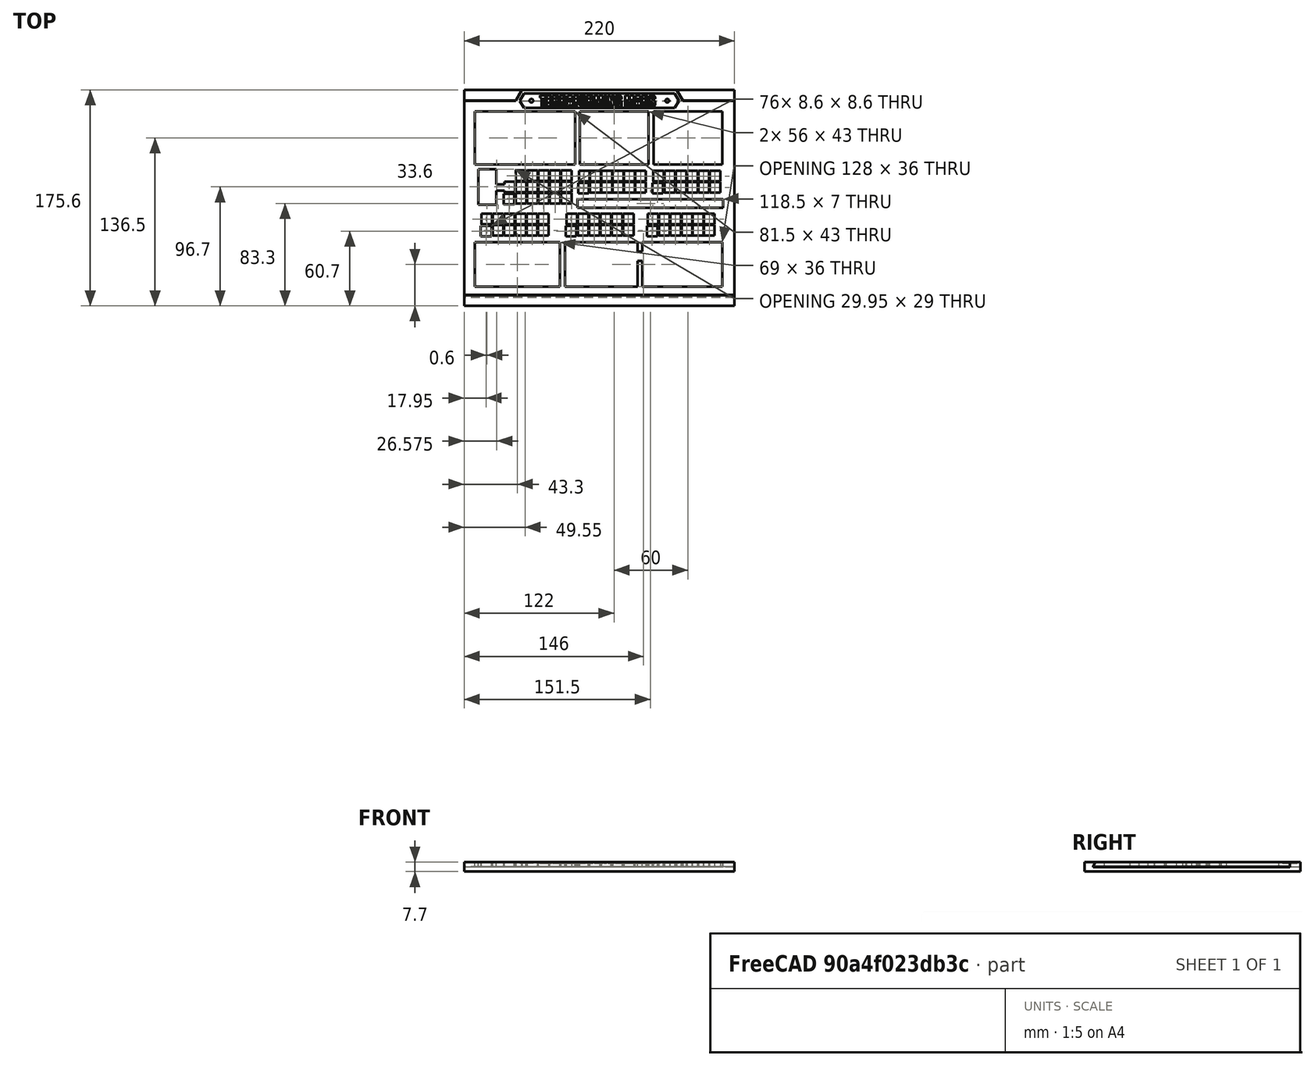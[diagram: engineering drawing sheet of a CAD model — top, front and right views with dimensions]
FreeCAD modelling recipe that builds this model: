
FCSTD DOCUMENT  (FreeCAD 0.21R33668 +26 (Git))
Label: overlay-full-v4
License: All rights reserved
LicenseURL: https://en.wikipedia.org/wiki/All_rights_reserved
objects: Sketcher::SketchObject×9, PartDesign::Pad×9, PartDesign::Pocket×4, Part::Feature×2, PartDesign::Body×2, Mesh::Feature×1, Part::Refine×1, PartDesign::FeatureBase×1, Part::Part2DObjectPython×1, Part::Extrusion×1
note: 43 computed .brp shape members not serialized (recipe doc carries the construction recipe); baked Part::Feature solids carry a one-line shape summary decoded from their .brp

FEATURE [Mesh::Feature] Terraforming_Mars_overlay
FEATURE [Part::Feature] Terraforming_Mars_overlay001
  shape: bbox 208 x 148 x 3.7 mm, 1736 faces, 0 solids (baked)
FEATURE [Part::Feature] Terraforming_Mars_overlay001_solid  label="Terraforming_Mars_overlay001 (Solid)"
  shape: bbox 208 x 148 x 3.7 mm, 1736 faces (baked)
FEATURE [Part::Refine] Terraforming_Mars_overlay001_solid001  label="Terraforming_Mars_overlay001 (Solid)001"
  Source = -> Terraforming_Mars_overlay001_solid
FEATURE [PartDesign::FeatureBase] BaseFeature
  BaseFeature = -> Terraforming_Mars_overlay001_solid001
FEATURE [Sketcher::SketchObject] Sketch
  ExternalGeometry = -> [BaseFeature]
  FullyConstrained = true
  MapMode = 5
  Placement = pos=(0,0,3.7) rot=(0,0,1;0rad)
  Support = -> [BaseFeature]
  sketch-geometry (8):
    g0: LineSegment StartX=6 StartY=154 StartZ=0 EndX=214 EndY=154 EndZ=0
    g1: LineSegment StartX=214 StartY=154 StartZ=0 EndX=214 EndY=6 EndZ=0
    g2: LineSegment StartX=214 StartY=6 StartZ=0 EndX=6 EndY=6 EndZ=0
    g3: LineSegment StartX=6 StartY=6 StartZ=0 EndX=6 EndY=154 EndZ=0
    g4: LineSegment StartX=0 StartY=160 StartZ=0 EndX=220 EndY=160 EndZ=0
    g5: LineSegment StartX=220 StartY=160 StartZ=0 EndX=220 EndY=0 EndZ=0
    g6: LineSegment StartX=220 StartY=0 StartZ=0 EndX=0 EndY=0 EndZ=0
    g7: LineSegment StartX=0 StartY=0 StartZ=0 EndX=0 EndY=160 EndZ=0
  constraints (22):
    c: Coincident(g0,g1)
    c: Coincident(g1,g2)
    c: Coincident(g2,g3)
    c: Coincident(g3,g0)
    c: Horizontal(g0)
    c: Horizontal(g2)
    c: Vertical(g1)
    c: Vertical(g3)
    c: Coincident(g0,g-3)
    c: Coincident(g1,g-4)
    c: Coincident(g4,g5)
    c: Coincident(g5,g6)
    c: Coincident(g6,g7)
    c: Coincident(g7,g4)
    c: Horizontal(g4)
    c: Horizontal(g6)
    c: Vertical(g5)
    c: Vertical(g7)
    c: DistanceX(g4,g0) = 6
    c: DistanceX(g0,g4) = 6
    c: DistanceY(g0,g4) = 6
    c: DistanceY(g5,g1) = 6
FEATURE [PartDesign::Pad] Pad
  BaseFeature = -> BaseFeature
  Direction = (0,0,1)
  Length = 10
  Length2 = 10
  Profile = -> Sketch
  ReferenceAxis = -> Sketch [N_Axis]
  Type = 3
  UpToFace = -> BaseFeature [Face1]
FEATURE [Sketcher::SketchObject] Sketch001
  ExternalGeometry = -> [Pad]
  FullyConstrained = true
  MapMode = 5
  Placement = pos=(0,0,3.7) rot=(0,0,1;0rad)
  Support = -> [Pad]
  sketch-geometry (5):
    g0: GeomPoint X=110 Y=160 Z=0
    g1: LineSegment StartX=42 StartY=160 StartZ=0 EndX=47.0807 EndY=168.8 EndZ=0
    g2: LineSegment StartX=47.0807 StartY=168.8 StartZ=0 EndX=172.919 EndY=168.8 EndZ=0
    g3: LineSegment StartX=172.919 StartY=168.8 StartZ=0 EndX=178 EndY=160 EndZ=0
    g4: LineSegment StartX=178 StartY=160 StartZ=0 EndX=42 EndY=160 EndZ=0
  constraints (13):
    c: Symmetric(g-3,g-3,g0)
    c: Coincident(g1,g2)
    c: Horizontal(g2)
    c: Coincident(g2,g3)
    c: Coincident(g3,g4)
    c: Coincident(g4,g1)
    c: Angle(g1,g4,g1) = 2.0944
    c: Angle(g4,g3,g3) = 2.0944
    c: DistanceY(g1,g1) = 8.8
    c: PointOnObject(g1,g-3)
    c: DistanceX(g-3,g1) = 42
    c: DistanceX(g3,g-3) = 42
    c: PointOnObject(g3,g-3)
FEATURE [PartDesign::Pad] Pad001
  BaseFeature = -> Pad
  Direction = (0,0,1)
  Length = 10
  Length2 = 10
  Profile = -> Sketch001
  ReferenceAxis = -> Sketch001 [N_Axis]
  Type = 3
  UpToFace = -> Pad [Face2]
FEATURE [Sketcher::SketchObject] Sketch002
  ExternalGeometry = -> [Pad001]
  FullyConstrained = true
  MapMode = 5
  Placement = pos=(0,0,3.7) rot=(0,0,1;0rad)
  Support = -> [Pad001]
  sketch-geometry (7):
    g0: GeomPoint X=110 Y=160 Z=0
    g1: LineSegment StartX=45.2332 StartY=160 StartZ=0 EndX=48.6973 EndY=166 EndZ=0
    g2: LineSegment StartX=48.6973 StartY=166 StartZ=0 EndX=171.303 EndY=166 EndZ=0
    g3: LineSegment StartX=171.303 StartY=166 StartZ=0 EndX=174.767 EndY=160 EndZ=0
    g4: LineSegment StartX=174.767 StartY=160 StartZ=0 EndX=171.303 EndY=154 EndZ=0
    g5: LineSegment StartX=171.303 StartY=154 StartZ=0 EndX=48.6973 EndY=154 EndZ=0
    g6: LineSegment StartX=48.6973 StartY=154 StartZ=0 EndX=45.2332 EndY=160 EndZ=0
  constraints (17):
    c: Symmetric(g-4,g-4,g0)
    c: PointOnObject(g1,g-4)
    c: Coincident(g1,g2)
    c: Horizontal(g2)
    c: Coincident(g2,g3)
    c: PointOnObject(g3,g-4)
    c: Coincident(g3,g4)
    c: PointOnObject(g4,g-5)
    c: Coincident(g4,g5)
    c: Coincident(g5,g6)
    c: Coincident(g6,g1)
    c: Parallel(g1,g-6)
    c: Symmetric(g5,g1,g-4)
    c: Symmetric(g4,g2,g-4)
    c: Parallel(g3,g-7)
    c: Distance(g1,g-6) = 2.8
    c: Distance(g2,g-7) = 2.8
FEATURE [PartDesign::Pocket] Pocket
  BaseFeature = -> Pad001
  Direction = (0,0,-1)
  Length = 1
  Length2 = 5
  Profile = -> Sketch002
  ReferenceAxis = -> Sketch002 [N_Axis]
  Type = 0
FEATURE [Part::Part2DObjectPython] ShapeString  # Draft 2D object (typed FeaturePython)
  FontFile = <path>
  MakeFace = true
  Placement = pos=(61.7,155.5,2.7) rot=(0,0,1;0rad)
  Size = 9
  String = TERRAFORMING MARS
  Tracking = 0
FEATURE [Sketcher::SketchObject] Sketch003
  ExternalGeometry = -> [Pocket]
  FullyConstrained = true
  MapMode = 5
  Placement = pos=(0,0,2.7) rot=(0,0,1;0rad)
  Support = -> [Pocket]
  sketch-geometry (3):
    g0: LineSegment StartX=45.2332 StartY=160 StartZ=0 EndX=174.767 EndY=160 EndZ=0
    g1: Circle CenterX=54.7332 CenterY=160 CenterZ=0 NormalX=0 NormalY=0 NormalZ=1 AngleXU=0 Radius=1.5
    g2: Circle CenterX=165.267 CenterY=160 CenterZ=0 NormalX=0 NormalY=0 NormalZ=1 AngleXU=0 Radius=1.5
  constraints (8):
    c: Coincident(g0,g-3)
    c: Coincident(g0,g-4)
    c: PointOnObject(g1,g0)
    c: PointOnObject(g2,g0)
    c: Diameter(g2) = 3
    c: Diameter(g1) = 3
    c: DistanceX(g0,g1) = 9.5
    c: DistanceX(g2,g0) = 9.5
FEATURE [PartDesign::Pad] Pad002
  BaseFeature = -> Pocket
  Direction = (0,0,1)
  Length = 1
  Length2 = 10
  Profile = -> Sketch003
  ReferenceAxis = -> Sketch003 [N_Axis]
  Type = 0
FEATURE [Part::Extrusion] Extrude  label="Text"
  Base = -> ShapeString
  Dir = (0,0,1)
  DirMode = 2
  FaceMakerClass = Part::FaceMakerBullseye
  LengthFwd = 1
  LengthRev = 0
  Solid = false
  Symmetric = false
FEATURE [Sketcher::SketchObject] Sketch005
  FullyConstrained = true
  MapMode = 5
  Support = -> [XY_Plane001]
  sketch-geometry (4):
    g0: LineSegment StartX=0 StartY=160 StartZ=0 EndX=220 EndY=160 EndZ=0
    g1: LineSegment StartX=220 StartY=160 StartZ=0 EndX=220 EndY=0 EndZ=0
    g2: LineSegment StartX=220 StartY=0 StartZ=0 EndX=0 EndY=0 EndZ=0
    g3: LineSegment StartX=0 StartY=0 StartZ=0 EndX=0 EndY=160 EndZ=0
  constraints (12):
    c: Coincident(g0,g1)
    c: Coincident(g1,g2)
    c: Coincident(g2,g3)
    c: Coincident(g3,g0)
    c: Horizontal(g0)
    c: Horizontal(g2)
    c: Vertical(g1)
    c: Vertical(g3)
    c: PointOnObject(g1,g-1)
    c: PointOnObject(g0,g-2)
    c: DistanceX(g0,g0) = 220
    c: DistanceY(g1,g1) = 160
FEATURE [PartDesign::Pad] Pad004
  Direction = (0,0,1)
  Length = 4
  Length2 = 10
  Profile = -> Sketch005
  ReferenceAxis = -> Sketch005 [N_Axis]
  Reversed = true
  Type = 0
FEATURE [PartDesign::Pad] Pad005
  BaseFeature = -> Pad004
  Direction = (0,-1,0)
  Length = 6.8
  Length2 = 10
  Profile = -> Pad004 [Face3]
  Type = 0
FEATURE [PartDesign::Pad] Pad006
  BaseFeature = -> Pad005
  Direction = (0,0,1)
  Length = 3.7
  Length2 = 10
  Profile = -> Pad005 [Face8]
  Type = 0
FEATURE [PartDesign::Pad] Pad007
  BaseFeature = -> Pad006
  Direction = (0,1,0)
  Length = 2
  Length2 = 10
  Profile = -> Pad006 [Face8]
  Type = 0
FEATURE [Sketcher::SketchObject] Sketch006
  ExternalGeometry = -> [Pad007]
  FullyConstrained = true
  MapMode = 5
  Placement = pos=(220,0,0) rot=(0.57735,0.57735,0.57735;2.0944rad)
  Support = -> [Pad007]
  sketch-geometry (4):
    g0: LineSegment StartX=-0.1 StartY=0 StartZ=0 EndX=2 EndY=0 EndZ=0
    g1: LineSegment StartX=2 StartY=0 StartZ=0 EndX=2 EndY=3.7 EndZ=0
    g2: LineSegment StartX=-0.1 StartY=0 StartZ=0 EndX=1.9 EndY=3.7 EndZ=0
    g3: LineSegment StartX=1.9 StartY=3.7 StartZ=0 EndX=2 EndY=3.7 EndZ=0
  constraints (10):
    c: PointOnObject(g0,g-1)
    c: Coincident(g0,g-5)
    c: Coincident(g1,g0)
    c: DistanceX(g0,g0) = 2.1
    c: Coincident(g2,g0)
    c: PointOnObject(g2,g-4)
    c: Coincident(g3,g2)
    c: Coincident(g3,g1)
    c: DistanceX(g3,g3) = 0.1
    c: Coincident(g1,g-5)
FEATURE [PartDesign::Pocket] Pocket002
  BaseFeature = -> Pad007
  Direction = (-1,0,0)
  Length = 5
  Length2 = 5
  Profile = -> Sketch006
  ReferenceAxis = -> Sketch006 [N_Axis]
  Type = 1
FEATURE [PartDesign::Pad] Pad008
  BaseFeature = -> Pocket002
  Direction = (0,1,0)
  Length = 8.8
  Length2 = 10
  Profile = -> Pocket002 [Face1]
  Type = 0
FEATURE [Sketcher::SketchObject] Sketch007
  ExternalGeometry = -> [Pad008]
  FullyConstrained = true
  MapMode = 5
  Support = -> [Pad008]
  sketch-geometry (12):
    g0: LineSegment StartX=47.0807 StartY=168.8 StartZ=0 EndX=42 EndY=160 EndZ=0
    g1: LineSegment StartX=42 StartY=160 StartZ=0 EndX=0 EndY=160 EndZ=0
    g2: LineSegment StartX=0 StartY=168.8 StartZ=0 EndX=0 EndY=160.1 EndZ=0
    g3: LineSegment StartX=0 StartY=160.1 StartZ=0 EndX=41.9423 EndY=160.1 EndZ=0
    g4: LineSegment StartX=41.9423 StartY=160.1 StartZ=0 EndX=46.9652 EndY=168.8 EndZ=0
    g5: LineSegment StartX=46.9652 StartY=168.8 StartZ=0 EndX=0 EndY=168.8 EndZ=0
    g6: LineSegment StartX=220 StartY=160 StartZ=0 EndX=178 EndY=160 EndZ=0
    g7: LineSegment StartX=172.919 StartY=168.8 StartZ=0 EndX=178 EndY=160 EndZ=0
    g8: LineSegment StartX=173.035 StartY=168.8 StartZ=0 EndX=220 EndY=168.8 EndZ=0
    g9: LineSegment StartX=220 StartY=168.8 StartZ=0 EndX=220 EndY=160.1 EndZ=0
    g10: LineSegment StartX=220 StartY=160.1 StartZ=0 EndX=178.058 EndY=160.1 EndZ=0
    g11: LineSegment StartX=178.058 StartY=160.1 StartZ=0 EndX=173.035 EndY=168.8 EndZ=0
  constraints (34):
    c: PointOnObject(g0,g-4)
    c: PointOnObject(g0,g-3)
    c: Coincident(g0,g1)
    c: Coincident(g1,g-3)
    c: DistanceX(g1,g1) = 42
    c: Angle(g0,g-3,g0) = 2.0944
    c: Coincident(g-4,g2)
    c: PointOnObject(g2,g-2)
    c: Coincident(g2,g3)
    c: Horizontal(g3)
    c: Coincident(g3,g4)
    c: PointOnObject(g4,g-4)
    c: Coincident(g4,g5)
    c: Coincident(g5,g2)
    c: Distance(g2,g1) = 0.1
    c: Distance(g4,g0) = 0.1
    c: Parallel(g4,g0)
    c: Coincident(g6,g-3)
    c: PointOnObject(g6,g-3)
    c: PointOnObject(g7,g-4)
    c: Coincident(g7,g6)
    c: DistanceX(g6,g6) = 42
    c: Angle(g7,g-3,g6) = 1.0472
    c: PointOnObject(g8,g-4)
    c: Coincident(g8,g-4)
    c: Coincident(g8,g9)
    c: Vertical(g9)
    c: Coincident(g9,g10)
    c: Horizontal(g10)
    c: Coincident(g10,g11)
    c: Coincident(g11,g8)
    c: Distance(g9,g6) = 0.1
    c: Distance(g8,g7) = 0.1
    c: Parallel(g11,g7)
FEATURE [PartDesign::Pad] Pad009
  BaseFeature = -> Pad008
  Direction = (0,0,1)
  Length = 3.7
  Length2 = 10
  Profile = -> Sketch007
  ReferenceAxis = -> Sketch007 [N_Axis]
  Type = 0
FEATURE [Sketcher::SketchObject] Sketch008
  ExternalGeometry = -> [Pad009]
  FullyConstrained = true
  MapMode = 5
  Support = -> [Pad009]
  sketch-geometry (4):
    g0: LineSegment StartX=0 StartY=0 StartZ=0 EndX=220 EndY=0 EndZ=0
    g1: LineSegment StartX=220 StartY=0 StartZ=0 EndX=220 EndY=160 EndZ=0
    g2: LineSegment StartX=220 StartY=160 StartZ=0 EndX=0 EndY=160 EndZ=0
    g3: LineSegment StartX=0 StartY=160 StartZ=0 EndX=0 EndY=0 EndZ=0
  constraints (10):
    c: Coincident(g0,g1)
    c: Coincident(g1,g2)
    c: Coincident(g2,g3)
    c: Coincident(g3,g0)
    c: Horizontal(g0)
    c: Horizontal(g2)
    c: Vertical(g1)
    c: Vertical(g3)
    c: Coincident(g0,g-1)
    c: Coincident(g1,g-3)
FEATURE [PartDesign::Pocket] Pocket003
  BaseFeature = -> Pad009
  Direction = (0,0,-1)
  Length = 0.3
  Length2 = 5
  Profile = -> Sketch008
  ReferenceAxis = -> Sketch008 [N_Axis]
  Type = 0
FEATURE [PartDesign::Body] Body001  label="Back"
  Group = -> [Sketch005,Pad004,Pad005,Pad006,Pad007,Sketch006,Pocket002,Pad008,Sketch007,Pad009,Sketch008,Pocket003]
  Origin = -> Origin001
  Tip = -> Pocket003
FEATURE [Sketcher::SketchObject] Sketch009
  ExternalGeometry = -> [Pad002]
  FullyConstrained = true
  MapMode = 5
  Placement = pos=(220,0,0) rot=(0.57735,0.57735,0.57735;2.0944rad)
  Support = -> [Pad002]
  sketch-geometry (3):
    g0: LineSegment StartX=0 StartY=3.7 StartZ=0 EndX=0 EndY=0 EndZ=0
    g1: LineSegment StartX=0 StartY=0 StartZ=0 EndX=2 EndY=3.7 EndZ=0
    g2: LineSegment StartX=2 StartY=3.7 StartZ=0 EndX=0 EndY=3.7 EndZ=0
  constraints (7):
    c: Coincident(g-3,g0)
    c: Coincident(g0,g-1)
    c: Coincident(g0,g1)
    c: PointOnObject(g1,g-3)
    c: Coincident(g1,g2)
    c: Coincident(g2,g0)
    c: DistanceX(g2,g2) = 2
FEATURE [PartDesign::Pocket] Pocket004
  BaseFeature = -> Pad002
  Direction = (-1,0,0)
  Length = 5
  Length2 = 5
  Profile = -> Sketch009
  ReferenceAxis = -> Sketch009 [N_Axis]
  Type = 1
FEATURE [PartDesign::Body] Body  label="Front"
  BaseFeature = -> Terraforming_Mars_overlay001_solid001
  Group = -> [BaseFeature,Sketch,Pad,Sketch001,Pad001,Sketch002,Pocket,Sketch003,Pad002,Sketch009,Pocket004]
  Origin = -> Origin
  Tip = -> Pocket004
note: 1 file-system path scrubbed to <path> (originals preserved in the JSON sidecar)
